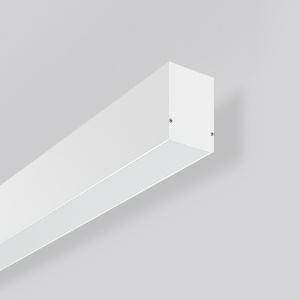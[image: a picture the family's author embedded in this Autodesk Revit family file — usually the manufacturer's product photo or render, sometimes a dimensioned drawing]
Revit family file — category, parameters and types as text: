
# Revit family: less_is_more_50_312608_002_1_76_a7a8
name_source: partatom
category: Lighting Fixtures
units: mm (PartAtom-declared; Revit-internal decimal feet)

## family parameters
Cut with Voids When Loaded = No
Host = Face
Light Source = No
Part Type = Normal
Room Calculation Point = No
Round Connector Dimension = Use Diameter
Shared = No

## types (1)
- LESS IS MORE 50 (1 x LED Modul 840, 2750 lm, 4000)
    Apparent Load = 20 VA
    CIE Flux Codes = 48 80 96 50 100
    Color Rendering = 80
    Color Temperature = 4000
    Default Elevation = 1800 mm
    Description = Series: LESS IS MORE 50
Linear wall luminaires. Housing: extruded aluminium profile, powder-coated. End cap aluminium powder-coated. Diffuser made of non-yellowing plastic (PMMA), opal. Direct 50%, indirect 50% light emission. Suitable for Wall (surface). LED unit with integrated converter interchangeable and removable. Suitable for through-wiring. With sensors or as a safety luminaire on request. 
Colour: traffic white, matt (RAL 9016)
Length: 1127 mm
Width: 67 mm
Height: 75 mm
Lamp: LED
Socket: without socket
Colour temperature: 4000K
Colour rendering index (CRI): 80
Light source: LED
Socket lamp2: Without base
Colour temperature: 4000K
Colour rendering index (CRI) 2: 80
System power: 20 W
Rated luminous flux: 2750 lm
Luminous efficiency: 138 lm/W
Control gear: Converter, dimmable, DALI
Control gear: Converter, dimmable, DALI
Protection class: I
Type of protection: IP 20
    Height = 75 mm
    Lamp = 1 x LED Modul 840
    Lamp Light Flux = 2750 lm
    Lamp count = 1
    Length = 1127 mm
    Lifetime = 50000 h
    Luminous efficacy = 138 lm/W
    Manufacturer = RZB
    ModVariant = No
    Model = 312608.002.1.76
    Mounting Place = Wall
    Mounting Type = Surface mounted
    Number of Poles = 1
    OnlyDefault = Yes
    Power Factor = 1
    Product Name = LESS IS MORE 50
    Product group = Surface mounted LED linear luminaires
    ProductGroupID = 2007
    Protection Class = Protection class I
    Protection Degree = IP 20
    RLX_Detail_Level = 1
    RLX_Emergency_Light_Flux = 0 lm
    RLX_Emergency_Type = 0
    RLX_Emergency_Type_DB = No
    RlxData = <blob elided: 39533 chars, md5=7937a8a6>
    Socket = socket
    Standby Power = 0 W
    System Light Flux = 2750 lm
    System Power = 20 W
    Type Comments = Product without accessories
    Type Image = 312606.002.jpg
    URL = http://relux.com
    VarID = ---
    Voltage = 0 V
    Weight = 0.00 kg
    Width = 67 mm

## geometry (parser evidence)
native form markers: Blend x4, Sweep x15
no freeform markers — native parametric forms only
